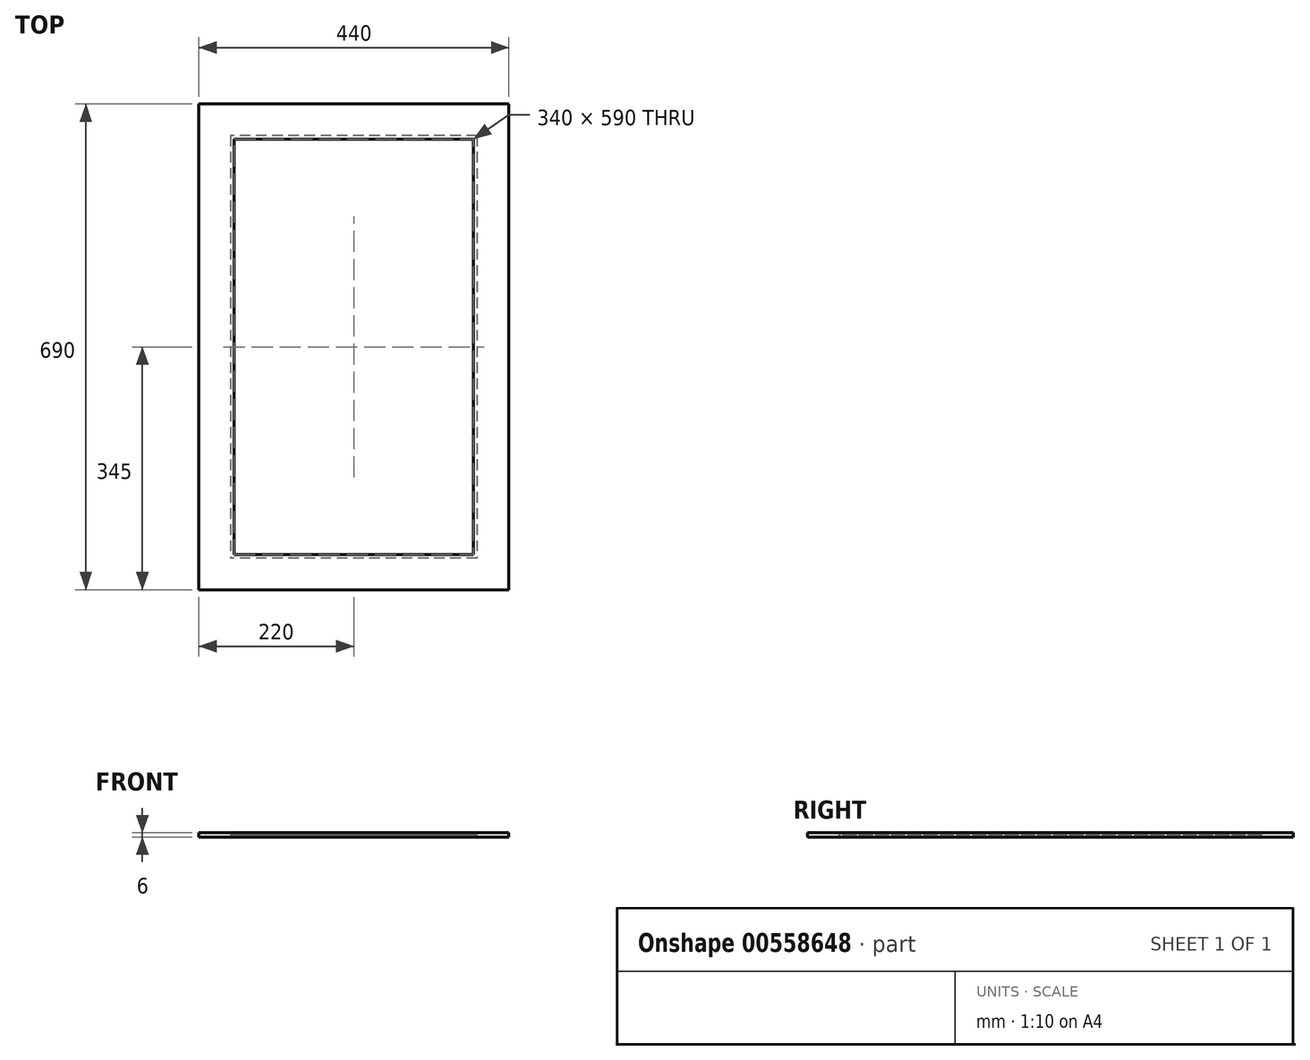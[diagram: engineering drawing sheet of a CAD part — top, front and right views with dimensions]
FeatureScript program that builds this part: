
annotation { "Feature Type Name" : "Feature", "Feature Type Description" : "" }
export const myFeature = defineFeature(function(context is Context, id is Id, definition is map)
    precondition{}
    {
        {
            var Q0;
            Q0=qCreatedBy(makeId("Top.planeOp"),FACE);
            var sketch = newSketch(context, id + "F0", { "sketchPlane" : qUnion([Q0])});
            skLineSegment(sketch, "E0.bottom", {"start": v(0, 0) * mm, "end": v(350, 0) * mm, "construction": true});
            skLineSegment(sketch, "E0.top", {"start": v(0, 600) * mm, "end": v(350, 600) * mm, "construction": true});
            skLineSegment(sketch, "E0.left", {"start": v(0, 0) * mm, "end": v(0, 600) * mm, "construction": true});
            skLineSegment(sketch, "E0.right", {"start": v(350, 0) * mm, "end": v(350, 600) * mm, "construction": true});
            skLineSegment(sketch, "E1.bottom", {"start": v(5, 595) * mm, "end": v(345, 595) * mm});
            skLineSegment(sketch, "E1.top", {"start": v(5, 5) * mm, "end": v(345, 5) * mm});
            skLineSegment(sketch, "E1.left", {"start": v(5, 595) * mm, "end": v(5, 5) * mm});
            skLineSegment(sketch, "E1.right", {"start": v(345, 595) * mm, "end": v(345, 5) * mm});
            skLineSegment(sketch, "E2.bottom", {"start": v(-45, 645) * mm, "end": v(395, 645) * mm});
            skLineSegment(sketch, "E2.top", {"start": v(-45, -45) * mm, "end": v(395, -45) * mm});
            skLineSegment(sketch, "E2.left", {"start": v(-45, 645) * mm, "end": v(-45, -45) * mm});
            skLineSegment(sketch, "E2.right", {"start": v(395, 645) * mm, "end": v(395, -45) * mm});
            skSolve(sketch);
        }
        {
            var Q0;
            Q0=makeQuery(id+"F0.imprint","IMPRINT",FACE,{"disambiguationData":[TD([[makeQuery(id+"F0.imprint","IMPRINT",EDGE,{"derivedFrom":sQuery(id+"F0.wireOp",EDGE,"E1.bottom")}),1.0]])]});
            extrude(context, id + "F1", {"entities" : qUnion([Q0]), "depth" : 6 * mm, "offsetDistance" : 25 * mm});
        }
        {
            var Q0;
            Q0=makeQuery(id+"F1.opExtrude","CAP_FACE",FACE,{"disambiguationData":[OSD([sQuery(id+"F0.wireOp",EDGE,"E1.bottom"),sQuery(id+"F0.wireOp",EDGE,"E1.top"),sQuery(id+"F0.wireOp",EDGE,"E1.left"),sQuery(id+"F0.wireOp",EDGE,"E1.right"),sQuery(id+"F0.wireOp",EDGE,"E2.bottom"),sQuery(id+"F0.wireOp",EDGE,"E2.top"),sQuery(id+"F0.wireOp",EDGE,"E2.left"),sQuery(id+"F0.wireOp",EDGE,"E2.right")])],"isStart":true});
            var sketch = newSketch(context, id + "F2", { "sketchPlane" : qUnion([Q0])});
            skLineSegment(sketch, "E3", {"start": v(175, -5) * mm, "end": v(175, 45) * mm, "construction": true});
            skLineSegment(sketch, "E4.bottom", {"start": v(350, -600) * mm, "end": v(0, -600) * mm});
            skLineSegment(sketch, "E4.top", {"start": v(350, 0) * mm, "end": v(0, 0) * mm});
            skLineSegment(sketch, "E4.left", {"start": v(350, -600) * mm, "end": v(350, 0) * mm});
            skLineSegment(sketch, "E4.right", {"start": v(0, -600) * mm, "end": v(0, 0) * mm});
            skLineSegment(sketch, "E5.bottom", {"start": v(225, 0) * mm, "end": v(125, 0) * mm});
            skLineSegment(sketch, "E5.top", {"start": v(225, 40) * mm, "end": v(125, 40) * mm});
            skLineSegment(sketch, "E5.left", {"start": v(225, 0) * mm, "end": v(225, 40) * mm});
            skLineSegment(sketch, "E5.right", {"start": v(125, 0) * mm, "end": v(125, 40) * mm});
            skSolve(sketch);
        }
        {
            var Q0;
            Q0=makeQuery(id+"F2.imprint","IMPRINT",FACE,{"disambiguationData":[TD([[makeQuery(id+"F2.imprint","IMPRINT",EDGE,{"derivedFrom":sQuery(id+"F2.wireOp",EDGE,"E5.bottom")}),-1.0]])]});
            var Q1;
            Q1=makeQuery(id+"F2.imprint","IMPRINT",FACE,{"disambiguationData":[TD([[makeQuery(id+"F2.imprint","IMPRINT",EDGE,{"derivedFrom":sQuery(id+"F2.wireOp",EDGE,"E4.bottom")}),-1.0]])]});
            extrude(context, id + "F3", {"entities" : qUnion([Q0, Q1]), "operationType" : NewBodyOperationType.REMOVE, "oppositeDirection" : true, "depth" : 3 * mm, "offsetDistance" : 25 * mm});
        }
    });
